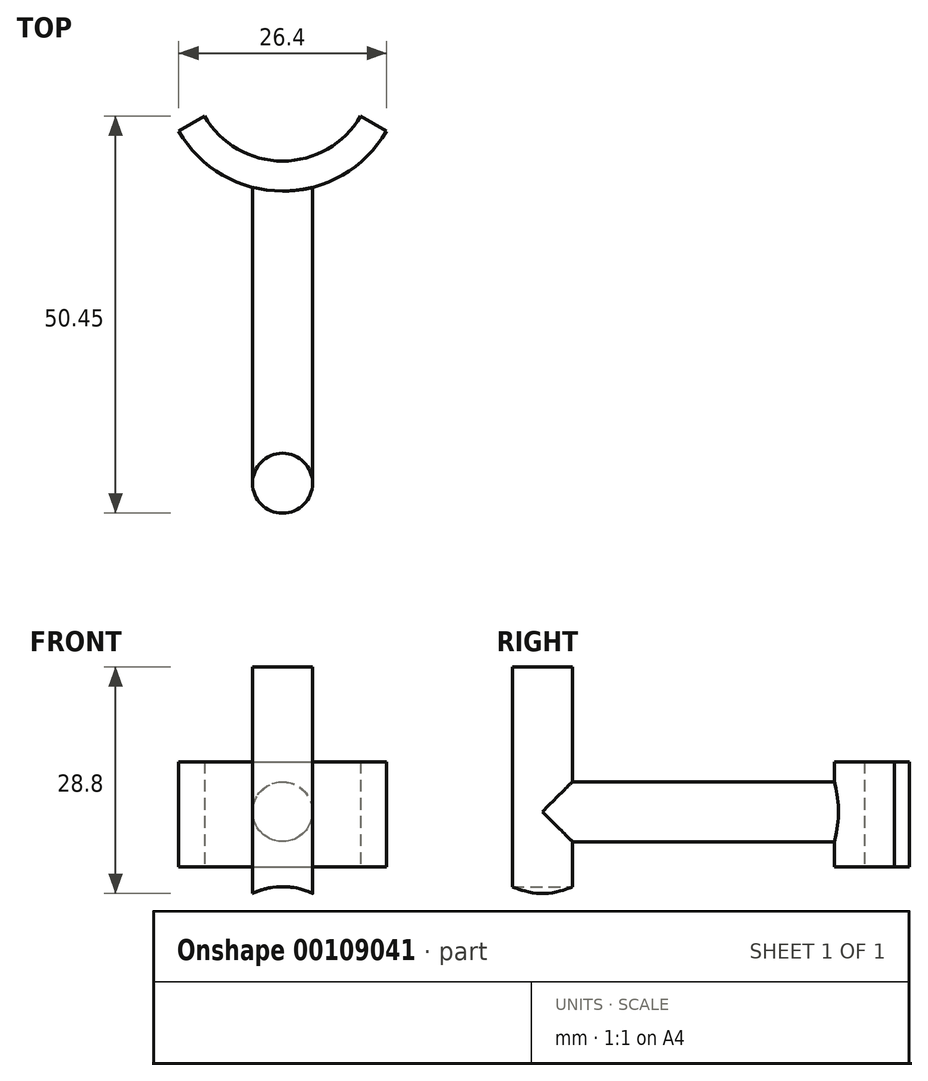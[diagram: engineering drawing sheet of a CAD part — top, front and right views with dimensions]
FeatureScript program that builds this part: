
annotation { "Feature Type Name" : "Feature", "Feature Type Description" : "" }
export const myFeature = defineFeature(function(context is Context, id is Id, definition is map)
    precondition{}
    {
        {
            var Q0;
            Q0=qCreatedBy(makeId("Front.planeOp"),FACE);
            var sketch = newSketch(context, id + "F0", { "sketchPlane" : qUnion([Q0])});
            skCircle(sketch, "E0", {"center": v(0, 0) * mm, "radius": 3.8 * mm});
            skSolve(sketch);
        }
        {
            var Q0;
            Q0=makeQuery(id+"F0.imprint","IMPRINT",FACE,{"disambiguationData":[TD([[makeQuery(id+"F0.imprint","IMPRINT",EDGE,{"derivedFrom":sQuery(id+"F0.wireOp",EDGE,"E0")}),1.0]])]});
            extrude(context, id + "F1", {"entities" : qUnion([Q0]), "depth" : 52.35 * mm});
        }
        {
            var Q0;
            Q0=qCreatedBy(makeId("Top.planeOp"),FACE);
            var sketch = newSketch(context, id + "F2", { "sketchPlane" : qUnion([Q0])});
            skCircle(sketch, "E1", {"center": v(0, 0) * mm, "radius": 11.43 * mm});
            skCircle(sketch, "E2", {"center": v(0, 0) * mm, "radius": 15.24 * mm});
            skLineSegment(sketch, "E3", {"start": v(0, 0) * mm, "end": v(-13.2, -7.62) * mm});
            skLineSegment(sketch, "E4", {"start": v(0, 0) * mm, "end": v(13.2, -7.62) * mm});
            skLineSegment(sketch, "E5", {"start": v(0, 0) * mm, "end": v(15.24, 0) * mm});
            skLineSegment(sketch, "E6", {"start": v(0, 0) * mm, "end": v(-15.24, 0) * mm});
            skSolve(sketch);
        }
        {
            var Q0;
            {var subQ0=sQuery(id+"F2.wireOp",EDGE,"E6");var subQ1=sQuery(id+"F2.wireOp",EDGE,"E1");var subQ2=makeQuery(id+"F2.imprint","INTERSECT",VERTEX,{"derivedFrom":[subQ1,subQ0]});Q0=makeQuery(id+"F2.imprint","IMPRINT",FACE,{"disambiguationData":[TD([[makeQuery(id+"F2.imprint","IMPRINT",EDGE,{"disambiguationData":[TD([[subQ2,-1.0]])],"derivedFrom":subQ1}),1.0]])]});}
            var Q1;
            {var subQ0=sQuery(id+"F2.wireOp",EDGE,"E3");var subQ1=sQuery(id+"F2.wireOp",EDGE,"E1");var subQ2=makeQuery(id+"F2.imprint","INTERSECT",VERTEX,{"derivedFrom":[subQ1,subQ0]});Q1=makeQuery(id+"F2.imprint","IMPRINT",FACE,{"disambiguationData":[TD([[makeQuery(id+"F2.imprint","IMPRINT",EDGE,{"disambiguationData":[TD([[subQ2,-1.0]])],"derivedFrom":subQ1}),1.0]])]});}
            var Q2;
            {var subQ0=sQuery(id+"F2.wireOp",EDGE,"E5");var subQ1=sQuery(id+"F2.wireOp",EDGE,"E1");var subQ2=makeQuery(id+"F2.imprint","INTERSECT",VERTEX,{"derivedFrom":[subQ1,subQ0]});Q2=makeQuery(id+"F2.imprint","IMPRINT",FACE,{"disambiguationData":[TD([[makeQuery(id+"F2.imprint","IMPRINT",EDGE,{"disambiguationData":[TD([[subQ2,1.0]])],"derivedFrom":subQ1}),1.0]])]});}
            extrude(context, id + "F3", {"entities" : qUnion([Q0, Q1, Q2]), "operationType" : NewBodyOperationType.REMOVE, "depth" : 25.4 * mm, "hasSecondDirection" : true, "secondDirectionOppositeDirection" : true, "secondDirectionDepth" : 25.4 * mm});
        }
        {
            var Q0;
            {var subQ0=sQuery(id+"F2.wireOp",EDGE,"E3");var subQ1=sQuery(id+"F2.wireOp",EDGE,"E1");var subQ2=makeQuery(id+"F2.imprint","INTERSECT",VERTEX,{"derivedFrom":[subQ1,subQ0]});Q0=makeQuery(id+"F2.imprint","IMPRINT",FACE,{"disambiguationData":[TD([[makeQuery(id+"F2.imprint","IMPRINT",EDGE,{"disambiguationData":[TD([[subQ2,-1.0]])],"derivedFrom":subQ1}),-1.0]])]});}
            extrude(context, id + "F4", {"entities" : qUnion([Q0]), "operationType" : NewBodyOperationType.ADD, "depth" : 6.35 * mm, "hasSecondDirection" : true, "secondDirectionOppositeDirection" : true, "secondDirectionDepth" : 7 * mm});
        }
        {
            var Q0;
            Q0=qCreatedBy(makeId("Top.planeOp"),FACE);
            var sketch = newSketch(context, id + "F5", { "sketchPlane" : qUnion([Q0])});
            skLineSegment(sketch, "E7", {"start": v(0, 0) * mm, "end": v(0, -52.35) * mm});
            skCircle(sketch, "E8", {"center": v(0, -52.35) * mm, "radius": 3.81 * mm});
            skSolve(sketch);
        }
        {
            var Q0;
            Q0=makeQuery(id+"F5.imprint","IMPRINT",FACE,{"disambiguationData":[TD([[makeQuery(id+"F5.imprint","IMPRINT",EDGE,{"derivedFrom":sQuery(id+"F5.wireOp",EDGE,"E8")}),1.0]])]});
            extrude(context, id + "F6", {"entities" : qUnion([Q0]), "operationType" : NewBodyOperationType.ADD, "depth" : 18.41 * mm, "hasSecondDirection" : true, "secondDirectionOppositeDirection" : true, "secondDirectionDepth" : 18.41 * mm});
        }
        {
            var Q0;
            Q0=qCreatedBy(makeId("Front.planeOp"),FACE);
            var sketch = newSketch(context, id + "F7", { "sketchPlane" : qUnion([Q0])});
            skCircle(sketch, "E9", {"center": v(0, -18.41) * mm, "radius": 8.9 * mm});
            skSolve(sketch);
        }
        {
            var Q0;
            Q0=makeQuery(id+"F7.imprint","IMPRINT",FACE,{"disambiguationData":[TD([[makeQuery(id+"F7.imprint","IMPRINT",EDGE,{"derivedFrom":sQuery(id+"F7.wireOp",EDGE,"E9")}),1.0]])]});
            extrude(context, id + "F8", {"entities" : qUnion([Q0]), "operationType" : NewBodyOperationType.REMOVE, "depth" : 66.63 * mm});
        }
    });
